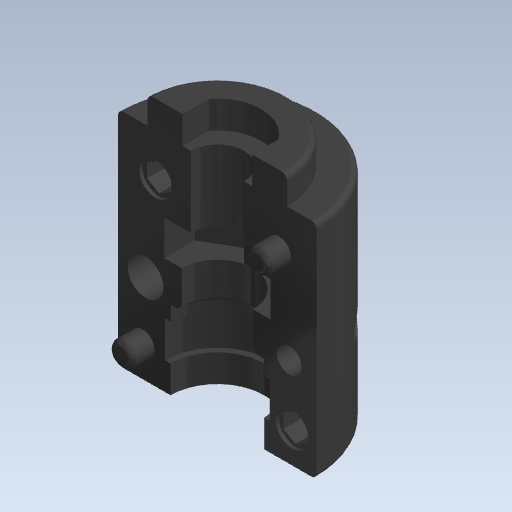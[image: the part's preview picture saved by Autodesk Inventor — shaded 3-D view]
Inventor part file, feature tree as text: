
AUTODESK INVENTOR PART (.ipt)
format: ipt  version: 2020 (Build 240168000, 168)  size: 194,560 bytes
history: native  units: mm (DEFAULTED — no unit token found)
features: fillet x1
ambient origin geometry x8: Origin, YZ Plane, XZ Plane, XY Plane, X Axis, Y Axis, Z Axis, Center Point
bodies: Solid1 (feature_tree)
feature tree (1):
  fillet  "Fillet1"  [1 undecoded]
note: 1 required parameter value undecoded (feature->parameter linkage not recoverable at this tier; creation-order binding heuristic only, values carry confidence <= 0.55)
